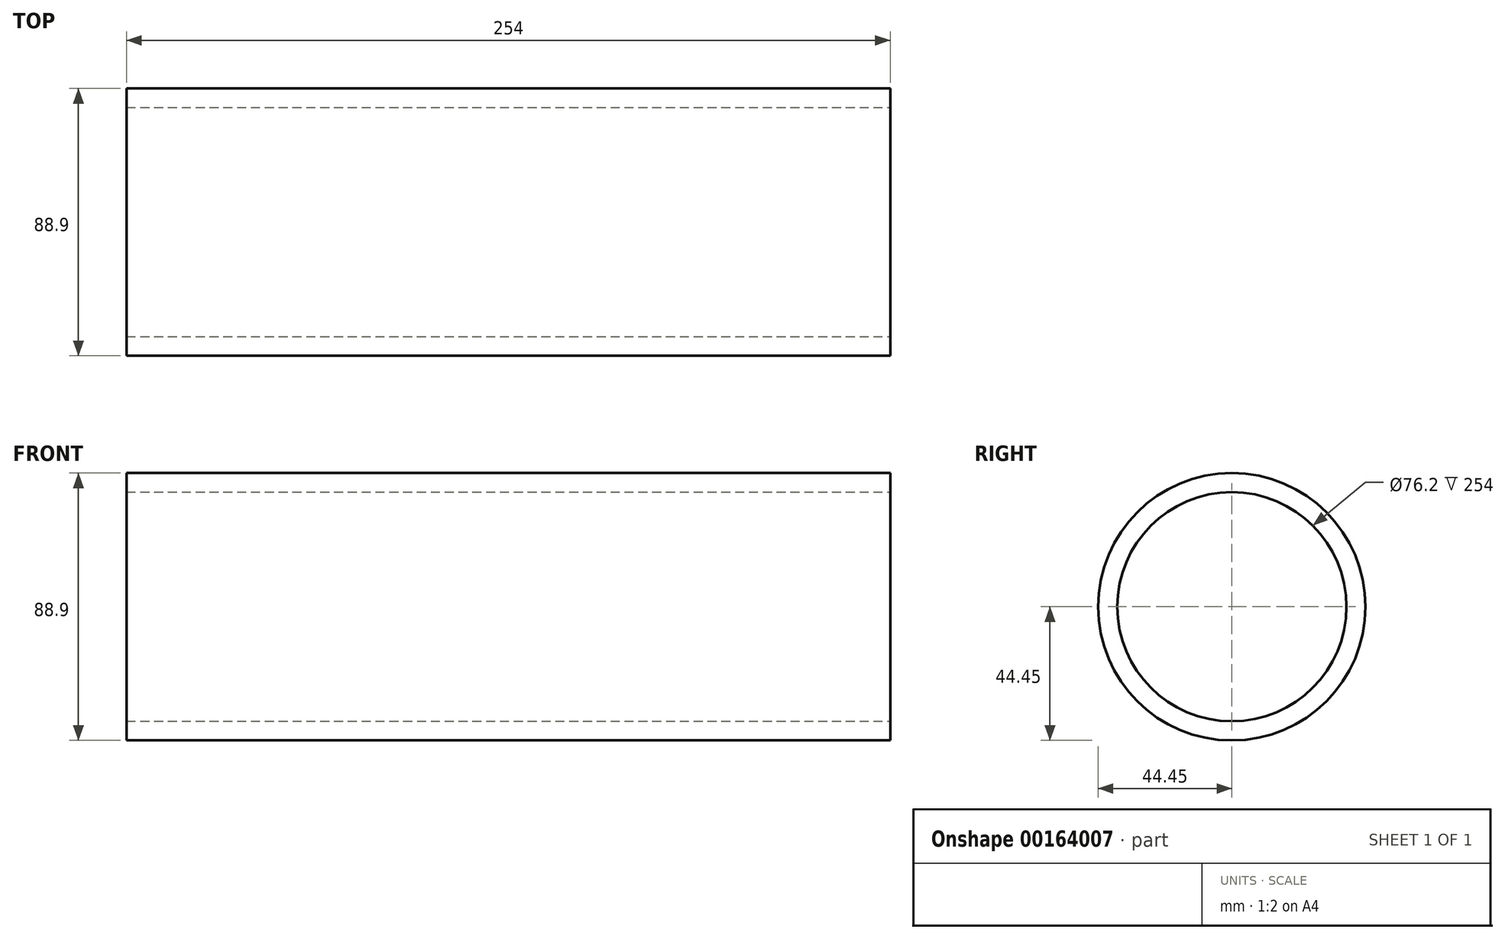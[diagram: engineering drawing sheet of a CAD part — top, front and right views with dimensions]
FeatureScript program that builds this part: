
annotation { "Feature Type Name" : "Feature", "Feature Type Description" : "" }
export const myFeature = defineFeature(function(context is Context, id is Id, definition is map)
    precondition{}
    {
        {
            var Q0;
            Q0=qCreatedBy(makeId("Right.planeOp"),FACE);
            var sketch = newSketch(context, id + "F0", { "sketchPlane" : qUnion([Q0])});
            skCircle(sketch, "E0", {"center": v(0, 0) * mm, "radius": 44.45 * mm});
            skCircle(sketch, "E1.0", {"center": v(0, 0) * mm, "radius": 38.1 * mm});
            skSolve(sketch);
        }
        {
            var Q0;
            Q0=makeQuery(id+"F0.imprint","IMPRINT",FACE,{"disambiguationData":[TD([[makeQuery(id+"F0.imprint","IMPRINT",EDGE,{"derivedFrom":sQuery(id+"F0.wireOp",EDGE,"E0")}),1.0]])]});
            extrude(context, id + "F1", {"entities" : qUnion([Q0]), "oppositeDirection" : true, "depth" : 254 * mm});
        }
    });
